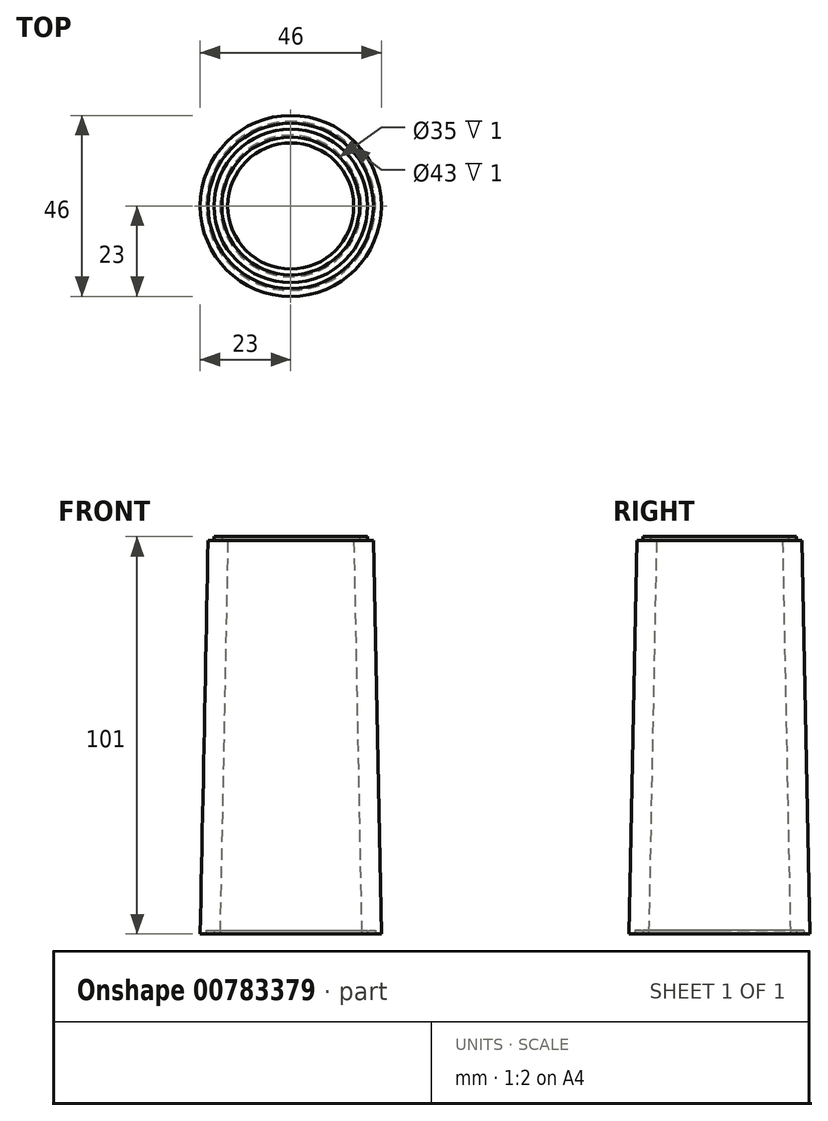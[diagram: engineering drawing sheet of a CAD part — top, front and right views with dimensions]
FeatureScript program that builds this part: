
annotation { "Feature Type Name" : "Feature", "Feature Type Description" : "" }
export const myFeature = defineFeature(function(context is Context, id is Id, definition is map)
    precondition{}
    {
        {
            var Q0;
            Q0=qCreatedBy(makeId("Front.planeOp"),FACE);
            var sketch = newSketch(context, id + "F0", { "sketchPlane" : qUnion([Q0])});
            skLineSegment(sketch, "E0", {"start": v(0, 0) * mm, "end": v(0, 167.63) * mm});
            skLineSegment(sketch, "E1", {"start": v(18, 0) * mm, "end": v(23, 0) * mm});
            skLineSegment(sketch, "E2", {"start": v(23, 0) * mm, "end": v(21, 100) * mm});
            skLineSegment(sketch, "E3", {"start": v(21, 100) * mm, "end": v(16, 100) * mm});
            skLineSegment(sketch, "E4", {"start": v(16, 100) * mm, "end": v(18, 0) * mm});
            skLineSegment(sketch, "E5", {"start": v(16, 100) * mm, "end": v(17.5, 100) * mm});
            skLineSegment(sketch, "E6", {"start": v(17.5, 100) * mm, "end": v(17.5, 101) * mm});
            skLineSegment(sketch, "E7", {"start": v(17.5, 101) * mm, "end": v(19.5, 101) * mm});
            skLineSegment(sketch, "E8", {"start": v(19.5, 101) * mm, "end": v(19.5, 100) * mm});
            skLineSegment(sketch, "E9", {"start": v(19.5, 100) * mm, "end": v(21, 100) * mm});
            skLineSegment(sketch, "E10", {"start": v(18, 0) * mm, "end": v(19.5, 0) * mm});
            skLineSegment(sketch, "E11", {"start": v(19.5, 0) * mm, "end": v(19.5, 1) * mm});
            skLineSegment(sketch, "E12", {"start": v(19.5, 1) * mm, "end": v(21.5, 1) * mm});
            skLineSegment(sketch, "E13", {"start": v(21.5, 1) * mm, "end": v(21.5, 0) * mm});
            skLineSegment(sketch, "E14", {"start": v(21.5, 0) * mm, "end": v(23, 0) * mm});
            skSolve(sketch);
        }
        {
            var Q0;
            {var subQ3=sQuery(id+"F0.wireOp",EDGE,"E2");Q0=makeQuery(id+"F0.imprint","IMPRINT",FACE,{"disambiguationData":[TD([[makeQuery(id+"F0.imprint","IMPRINT",EDGE,{"derivedFrom":subQ3}),1.0]])]});}
            var Q1;
            {var subQ2=sQuery(id+"F0.wireOp",EDGE,"E6");Q1=makeQuery(id+"F0.imprint","IMPRINT",FACE,{"disambiguationData":[TD([[makeQuery(id+"F0.imprint","IMPRINT",EDGE,{"derivedFrom":subQ2}),-1.0]])]});}
            var Q2;
            Q2=sQuery(id+"F0.wireOp",EDGE,"E0");
            revolve(context, id + "F1", {"surfaceOperationType" : NewSurfaceOperationType.NEW, "entities" : qUnion([Q0, Q1]), "axis" : qUnion([Q2]), "revolveType" : RevolveType.FULL});
        }
        {
            var Q0;
            {var subQ0=sQuery(id+"F0.wireOp",EDGE,"E11");Q0=makeQuery(id+"F0.imprint","IMPRINT",FACE,{"disambiguationData":[TD([[makeQuery(id+"F0.imprint","IMPRINT",EDGE,{"derivedFrom":subQ0}),-1.0]])]});}
            var Q1;
            Q1=sQuery(id+"F0.wireOp",EDGE,"E0");
            revolve(context, id + "F2", {"operationType" : NewBodyOperationType.REMOVE, "surfaceOperationType" : NewSurfaceOperationType.NEW, "entities" : qUnion([Q0]), "axis" : qUnion([Q1]), "revolveType" : RevolveType.FULL, "oppositeDirection" : true});
        }
    });
